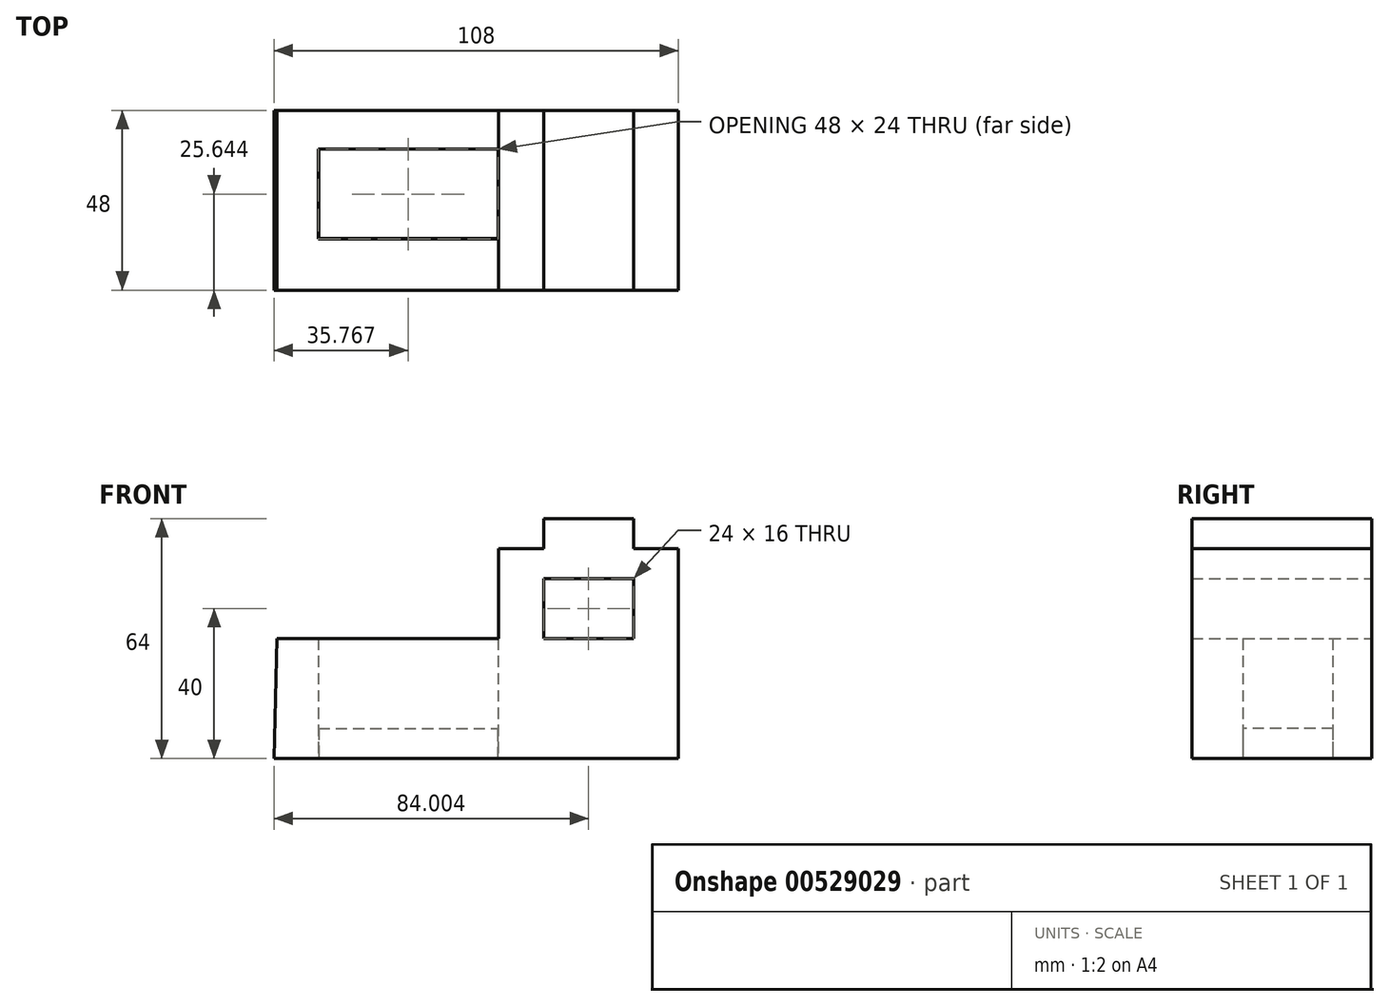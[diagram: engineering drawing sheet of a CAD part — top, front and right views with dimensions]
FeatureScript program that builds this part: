
annotation { "Feature Type Name" : "Feature", "Feature Type Description" : "" }
export const myFeature = defineFeature(function(context is Context, id is Id, definition is map)
    precondition{}
    {
        {
            var Q0;
            Q0=qCreatedBy(makeId("Front.planeOp"),FACE);
            var sketch = newSketch(context, id + "F0", { "sketchPlane" : qUnion([Q0])});
            skLineSegment(sketch, "E0", {"start": v(-50.62, 0) * mm, "end": v(57.38, 0) * mm});
            skLineSegment(sketch, "E1", {"start": v(57.38, 0) * mm, "end": v(57.38, 56) * mm});
            skLineSegment(sketch, "E2", {"start": v(57.38, 56) * mm, "end": v(45.38, 56) * mm});
            skLineSegment(sketch, "E3", {"start": v(45.38, 56) * mm, "end": v(45.38, 64) * mm});
            skLineSegment(sketch, "E4", {"start": v(45.38, 64) * mm, "end": v(21.38, 64) * mm});
            skLineSegment(sketch, "E5", {"start": v(21.38, 64) * mm, "end": v(21.38, 56) * mm});
            skLineSegment(sketch, "E6", {"start": v(21.38, 56) * mm, "end": v(9.38, 56) * mm});
            skLineSegment(sketch, "E7", {"start": v(9.38, 56) * mm, "end": v(9.38, 32) * mm});
            skLineSegment(sketch, "E8", {"start": v(9.38, 32) * mm, "end": v(-49.86, 32) * mm});
            skLineSegment(sketch, "E9", {"start": v(-49.86, 32) * mm, "end": v(-50.62, 0) * mm});
            skLineSegment(sketch, "E10", {"start": v(21.38, 48) * mm, "end": v(45.38, 48) * mm});
            skLineSegment(sketch, "E11", {"start": v(45.38, 48) * mm, "end": v(45.38, 32) * mm});
            skLineSegment(sketch, "E12", {"start": v(45.38, 32) * mm, "end": v(21.38, 32) * mm});
            skLineSegment(sketch, "E13", {"start": v(21.38, 32) * mm, "end": v(21.38, 48) * mm});
            skSolve(sketch);
        }
        {
            var Q0;
            Q0=makeQuery(id+"F0.imprint","IMPRINT",FACE,{"disambiguationData":[TD([[makeQuery(id+"F0.imprint","IMPRINT",EDGE,{"derivedFrom":sQuery(id+"F0.wireOp",EDGE,"E0")}),1.0]])]});
            extrude(context, id + "F1", {"entities" : qUnion([Q0]), "depth" : 48 * mm, "offsetDistance" : 25 * mm});
        }
        {
            var Q0;
            Q0=qCreatedBy(makeId("Top.planeOp"),FACE);
            var sketch = newSketch(context, id + "F2", { "sketchPlane" : qUnion([Q0])});
            skLineSegment(sketch, "E14", {"start": v(9.15, -10.36) * mm, "end": v(9.15, -34.36) * mm});
            skLineSegment(sketch, "E15", {"start": v(9.15, -34.36) * mm, "end": v(-38.85, -34.36) * mm});
            skLineSegment(sketch, "E16", {"start": v(-38.85, -34.36) * mm, "end": v(-38.85, -10.36) * mm});
            skLineSegment(sketch, "E17", {"start": v(-38.85, -10.36) * mm, "end": v(9.15, -10.36) * mm});
            skSolve(sketch);
        }
        {
            var Q0;
            Q0 = qSketchRegion(id + "F2", true);
            extrude(context, id + "F3", {"entities" : qUnion([Q0]), "operationType" : NewBodyOperationType.REMOVE, "endBound" : BoundingType.UP_TO_NEXT, "depth" : 25 * mm, "offsetDistance" : 25 * mm});
        }
        {
            var Q0;
            Q0=qCreatedBy(makeId("Top.planeOp"),FACE);
            var sketch = newSketch(context, id + "F4", { "sketchPlane" : qUnion([Q0])});
            skLineSegment(sketch, "E18", {"start": v(-38.72, -10.23) * mm, "end": v(-38.72, -34.23) * mm});
            skLineSegment(sketch, "E19", {"start": v(-38.72, -34.23) * mm, "end": v(9.28, -34.23) * mm});
            skLineSegment(sketch, "E20", {"start": v(9.28, -34.23) * mm, "end": v(9.28, -10.23) * mm});
            skLineSegment(sketch, "E21", {"start": v(9.28, -10.23) * mm, "end": v(-38.72, -10.23) * mm});
            skSolve(sketch);
        }
        {
            var Q0;
            Q0 = qSketchRegion(id + "F4", true);
            extrude(context, id + "F5", {"entities" : qUnion([Q0]), "operationType" : NewBodyOperationType.ADD, "depth" : 8 * mm, "offsetDistance" : 25 * mm});
        }
    });
